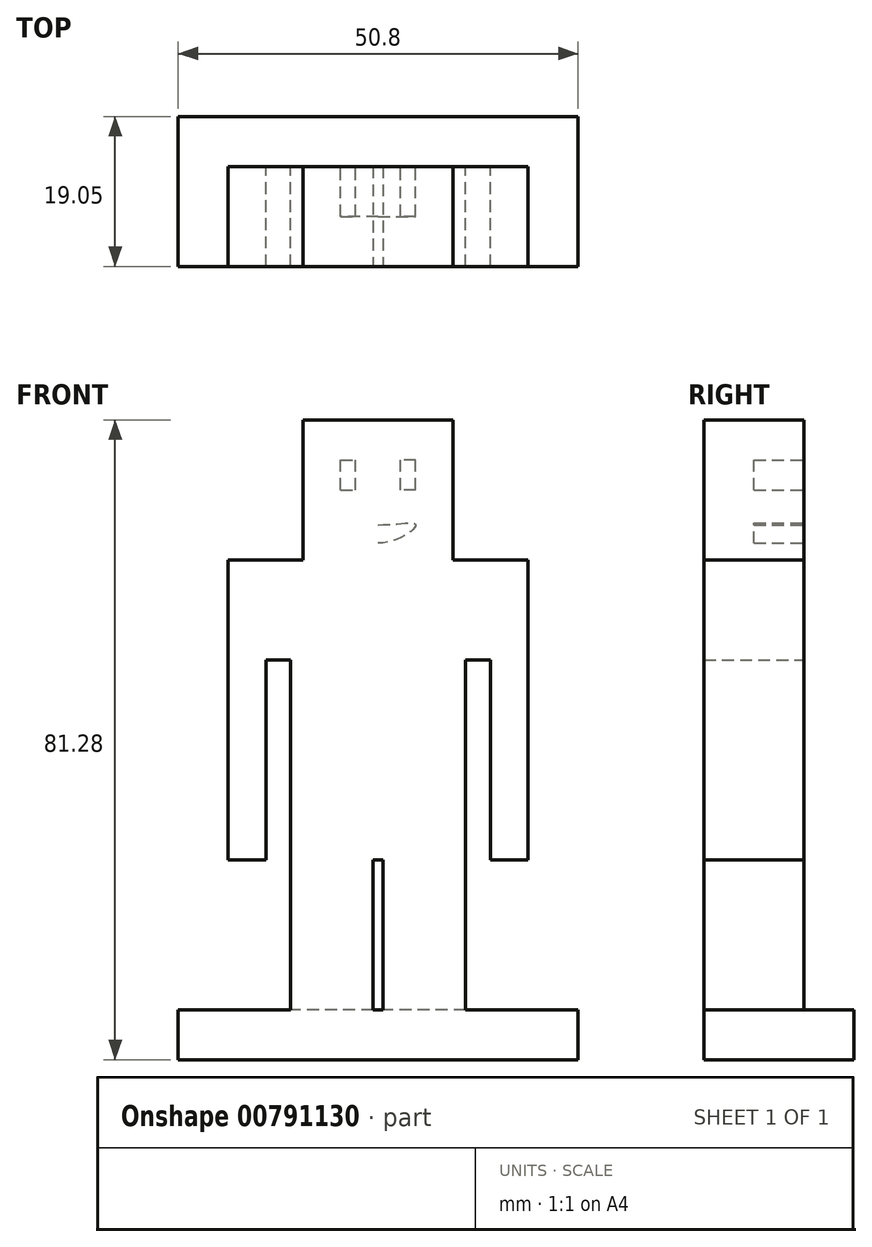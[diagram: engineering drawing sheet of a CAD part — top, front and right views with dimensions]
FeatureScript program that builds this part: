
annotation { "Feature Type Name" : "Feature", "Feature Type Description" : "" }
export const myFeature = defineFeature(function(context is Context, id is Id, definition is map)
    precondition{}
    {
        {
            var Q0;
            Q0=qCreatedBy(makeId("Top.planeOp"),FACE);
            var sketch = newSketch(context, id + "F0", { "sketchPlane" : qUnion([Q0])});
            skLineSegment(sketch, "E0", {"start": v(0, 0) * mm, "end": v(0, -25.4) * mm});
            skLineSegment(sketch, "E1", {"start": v(0, -25.4) * mm, "end": v(50.8, -25.4) * mm});
            skLineSegment(sketch, "E2", {"start": v(50.8, -25.4) * mm, "end": v(50.8, 0) * mm});
            skLineSegment(sketch, "E3", {"start": v(50.8, 0) * mm, "end": v(0, 0) * mm});
            skSolve(sketch);
        }
        {
            var Q0;
            Q0 = qSketchRegion(id + "F0", true);
            extrude(context, id + "F1", {"entities" : qUnion([Q0]), "depth" : 6.35 * mm, "offsetDistance" : 25.4 * mm});
        }
        {
            var Q0;
            Q0=makeQuery(id+"F1.opExtrude","CAP_FACE",FACE,{"disambiguationData":[OSD([sQuery(id+"F0.wireOp",EDGE,"E0"),sQuery(id+"F0.wireOp",EDGE,"E1"),sQuery(id+"F0.wireOp",EDGE,"E2"),sQuery(id+"F0.wireOp",EDGE,"E3")])],"isStart":false});
            var sketch = newSketch(context, id + "F2", { "sketchPlane" : qUnion([Q0])});
            skPoint(sketch, "E4", {"position": v(25.4, -12.7) * mm});
            skPoint(sketch, "E4.positionSnap0", {"position": v(25.4, 0) * mm});
            skPoint(sketch, "E4.positionSnap1", {"position": v(50.8, -12.7) * mm});
            skLineSegment(sketch, "E5.bottom", {"start": v(38.1, -6.35) * mm, "end": v(12.7, -6.35) * mm});
            skLineSegment(sketch, "E5.top", {"start": v(38.1, -19.05) * mm, "end": v(12.7, -19.05) * mm});
            skLineSegment(sketch, "E5.left", {"start": v(38.1, -6.35) * mm, "end": v(38.1, -19.05) * mm});
            skLineSegment(sketch, "E5.right", {"start": v(12.7, -6.35) * mm, "end": v(12.7, -19.05) * mm});
            skLineSegment(sketch, "E6", {"start": v(25.4, -19.05) * mm, "end": v(25.4, -6.35) * mm});
            skSolve(sketch);
        }
        {
            var Q0;
            Q0 = qSketchRegion(id + "F2", true);
            extrude(context, id + "F3", {"entities" : qUnion([Q0]), "operationType" : NewBodyOperationType.ADD, "depth" : 19.05 * mm, "offsetDistance" : 25.4 * mm});
        }
        {
            var Q0;
            Q0=makeQuery(id+"F3.opExtrude","CAP_FACE",FACE,{"disambiguationData":[OSD([sQuery(id+"F2.wireOp",EDGE,"E5.bottom"),sQuery(id+"F2.wireOp",EDGE,"E5.top"),sQuery(id+"F2.wireOp",EDGE,"E5.left"),sQuery(id+"F2.wireOp",EDGE,"E5.right")])],"isStart":false});
            cPlane(context, id + "F4", {"entities" : qUnion([Q0]), "cplaneType" : CPlaneType.OFFSET, "offset" : 0 * mm, "width" : 152.4 * mm, "height" : 152.4 * mm});
        }
        {
            var Q0;
            Q0=qCreatedBy(id+"F4.planeOp",FACE);
            var sketch = newSketch(context, id + "F5", { "sketchPlane" : qUnion([Q0])});
            skLineSegment(sketch, "E7.bottom", {"start": v(44.45, -6.35) * mm, "end": v(6.35, -6.35) * mm});
            skLineSegment(sketch, "E7.top", {"start": v(44.45, -19.05) * mm, "end": v(6.35, -19.05) * mm});
            skLineSegment(sketch, "E7.left", {"start": v(44.45, -6.35) * mm, "end": v(44.45, -19.05) * mm});
            skLineSegment(sketch, "E7.right", {"start": v(6.35, -6.35) * mm, "end": v(6.35, -19.05) * mm});
            skPoint(sketch, "E7.middle", {"position": v(25.4, -12.7) * mm});
            skSolve(sketch);
        }
        {
            var Q0;
            Q0=makeQuery(id+"F5.imprint","IMPRINT",FACE,{"disambiguationData":[TD([[makeQuery(id+"F5.imprint","IMPRINT",EDGE,{"derivedFrom":sQuery(id+"F5.wireOp",EDGE,"E7.bottom")}),1.0]])]});
            extrude(context, id + "F6", {"entities" : qUnion([Q0]), "operationType" : NewBodyOperationType.ADD, "depth" : 38.1 * mm, "offsetDistance" : 25.4 * mm});
        }
        {
            var Q0;
            Q0=makeQuery(id+"F6.opExtrude","CAP_FACE",FACE,{"disambiguationData":[OSD([sQuery(id+"F5.wireOp",EDGE,"E7.bottom"),sQuery(id+"F5.wireOp",EDGE,"E7.top"),sQuery(id+"F5.wireOp",EDGE,"E7.left"),sQuery(id+"F5.wireOp",EDGE,"E7.right")])],"isStart":false});
            var sketch = newSketch(context, id + "F7", { "sketchPlane" : qUnion([Q0])});
            skSolve(sketch);
        }
        {
            var Q0;
            Q0=makeQuery(id+"F7.imprint","IMPRINT",FACE,{"disambiguationData":[TD([[makeQuery(id+"F7.imprint","IMPRINT",EDGE,{"derivedFrom":makeQuery(id+"F6.opExtrude","CAP_EDGE",EDGE,{"disambiguationData":[OSD([sQuery(id+"F5.wireOp",EDGE,"E7.bottom")])],"isStart":false})}),1.0]])]});
            var sketch = newSketch(context, id + "F8", { "sketchPlane" : qUnion([Q0])});
            skLineSegment(sketch, "E8.bottom", {"start": v(34.92, -6.35) * mm, "end": v(15.87, -6.35) * mm});
            skLineSegment(sketch, "E8.top", {"start": v(34.92, -19.05) * mm, "end": v(15.88, -19.05) * mm});
            skLineSegment(sketch, "E8.left", {"start": v(34.92, -6.35) * mm, "end": v(34.92, -19.05) * mm});
            skLineSegment(sketch, "E8.right", {"start": v(15.87, -6.35) * mm, "end": v(15.88, -19.05) * mm});
            skPoint(sketch, "E8.middle", {"position": v(25.4, -12.7) * mm});
            skSolve(sketch);
        }
        {
            var Q0;
            Q0=makeQuery(id+"F8.imprint","IMPRINT",FACE,{"disambiguationData":[TD([[makeQuery(id+"F8.imprint","IMPRINT",EDGE,{"derivedFrom":sQuery(id+"F8.wireOp",EDGE,"E8.bottom")}),1.0]])]});
            extrude(context, id + "F9", {"entities" : qUnion([Q0]), "operationType" : NewBodyOperationType.ADD, "depth" : 17.78 * mm, "offsetDistance" : 25.4 * mm});
        }
        {
            var Q0;
            Q0=makeQuery(id+"F9.boolean.opBoolean","MERGE",FACE,{"derivedFrom":[makeQuery(id+"F6.boolean.opBoolean","MERGE",FACE,{"derivedFrom":[makeQuery(id+"F3.opExtrude","SWEPT_FACE",FACE,{"disambiguationData":[OSD([sQuery(id+"F2.wireOp",EDGE,"E5.top")])]}),makeQuery(id+"F6.opExtrude","SWEPT_FACE",FACE,{"disambiguationData":[OSD([sQuery(id+"F5.wireOp",EDGE,"E7.top")])]})]}),makeQuery(id+"F9.opExtrude","SWEPT_FACE",FACE,{"disambiguationData":[OSD([sQuery(id+"F8.wireOp",EDGE,"E8.top")])]})]});
            var sketch = newSketch(context, id + "F10", { "sketchPlane" : qUnion([Q0])});
            skLineSegment(sketch, "E9", {"start": v(25.4, 6.35) * mm, "end": v(25.4, 25.38) * mm});
            skLineSegment(sketch, "E10.bottom", {"start": v(26.04, 25.4) * mm, "end": v(24.77, 25.4) * mm});
            skLineSegment(sketch, "E10.top", {"start": v(26.04, 6.34) * mm, "end": v(24.77, 6.34) * mm});
            skLineSegment(sketch, "E10.left", {"start": v(26.04, 25.4) * mm, "end": v(26.04, 6.34) * mm});
            skLineSegment(sketch, "E10.right", {"start": v(24.77, 25.4) * mm, "end": v(24.77, 6.34) * mm});
            skPoint(sketch, "E10.middle", {"position": v(25.4, 15.87) * mm});
            skSolve(sketch);
        }
        {
            var Q0;
            Q0 = qSketchRegion(id + "F10", true);
            extrude(context, id + "F11", {"entities" : qUnion([Q0]), "operationType" : NewBodyOperationType.REMOVE, "oppositeDirection" : true, "depth" : 25.4 * mm, "offsetDistance" : 25.4 * mm});
        }
        {
            var Q0;
            Q0=makeQuery(id+"F9.boolean.opBoolean","MERGE",FACE,{"derivedFrom":[makeQuery(id+"F6.boolean.opBoolean","MERGE",FACE,{"derivedFrom":[makeQuery(id+"F3.opExtrude","SWEPT_FACE",FACE,{"disambiguationData":[OSD([sQuery(id+"F2.wireOp",EDGE,"E5.bottom")])]}),makeQuery(id+"F6.opExtrude","SWEPT_FACE",FACE,{"disambiguationData":[OSD([sQuery(id+"F5.wireOp",EDGE,"E7.bottom")])]})]}),makeQuery(id+"F9.opExtrude","SWEPT_FACE",FACE,{"disambiguationData":[OSD([sQuery(id+"F8.wireOp",EDGE,"E8.bottom")])]})]});
            var sketch = newSketch(context, id + "F12", { "sketchPlane" : qUnion([Q0])});
            skLineSegment(sketch, "E11", {"start": v(-38.1, 25.4) * mm, "end": v(-38.1, 50.8) * mm});
            skLineSegment(sketch, "E12", {"start": v(-12.7, 25.4) * mm, "end": v(-12.7, 50.8) * mm});
            skLineSegment(sketch, "E13.bottom", {"start": v(-36.51, 50.8) * mm, "end": v(-39.69, 50.8) * mm});
            skLineSegment(sketch, "E13.top", {"start": v(-36.51, 25.4) * mm, "end": v(-39.69, 25.4) * mm});
            skLineSegment(sketch, "E13.left", {"start": v(-36.51, 50.8) * mm, "end": v(-36.51, 25.4) * mm});
            skLineSegment(sketch, "E13.right", {"start": v(-39.69, 50.8) * mm, "end": v(-39.69, 25.4) * mm});
            skPoint(sketch, "E13.middle", {"position": v(-38.1, 38.1) * mm});
            skLineSegment(sketch, "E14.bottom", {"start": v(-11.16, 50.8) * mm, "end": v(-14.24, 50.8) * mm});
            skLineSegment(sketch, "E14.top", {"start": v(-11.16, 25.4) * mm, "end": v(-14.24, 25.4) * mm});
            skLineSegment(sketch, "E14.left", {"start": v(-11.16, 50.8) * mm, "end": v(-11.16, 25.4) * mm});
            skLineSegment(sketch, "E14.right", {"start": v(-14.24, 50.8) * mm, "end": v(-14.24, 25.4) * mm});
            skPoint(sketch, "E14.middle", {"position": v(-12.7, 38.1) * mm});
            skSolve(sketch);
        }
        {
            var Q0;
            {var subQ0=sQuery(id+"F12.wireOp",EDGE,"E11");Q0=makeQuery(id+"F12.imprint","IMPRINT",FACE,{"disambiguationData":[TD([[makeQuery(id+"F12.imprint","IMPRINT",EDGE,{"derivedFrom":subQ0}),1.0]])]});}
            var Q1;
            {var subQ0=sQuery(id+"F12.wireOp",EDGE,"E12");Q1=makeQuery(id+"F12.imprint","IMPRINT",FACE,{"disambiguationData":[TD([[makeQuery(id+"F12.imprint","IMPRINT",EDGE,{"derivedFrom":subQ0}),-1.0]])]});}
            var Q2;
            {var subQ0=sQuery(id+"F12.wireOp",EDGE,"E11");Q2=makeQuery(id+"F12.imprint","IMPRINT",FACE,{"disambiguationData":[TD([[makeQuery(id+"F12.imprint","IMPRINT",EDGE,{"derivedFrom":subQ0}),-1.0]])]});}
            var Q3;
            {var subQ0=sQuery(id+"F12.wireOp",EDGE,"E12");Q3=makeQuery(id+"F12.imprint","IMPRINT",FACE,{"disambiguationData":[TD([[makeQuery(id+"F12.imprint","IMPRINT",EDGE,{"derivedFrom":subQ0}),1.0]])]});}
            extrude(context, id + "F13", {"entities" : qUnion([Q0, Q1, Q2, Q3]), "operationType" : NewBodyOperationType.REMOVE, "oppositeDirection" : true, "depth" : 50.8 * mm, "offsetDistance" : 25.4 * mm});
        }
        {
            var Q0;
            Q0=makeQuery(id+"F9.boolean.opBoolean","MERGE",FACE,{"derivedFrom":[makeQuery(id+"F6.boolean.opBoolean","MERGE",FACE,{"derivedFrom":[makeQuery(id+"F3.opExtrude","SWEPT_FACE",FACE,{"disambiguationData":[OSD([sQuery(id+"F2.wireOp",EDGE,"E5.bottom")])]}),makeQuery(id+"F6.opExtrude","SWEPT_FACE",FACE,{"disambiguationData":[OSD([sQuery(id+"F5.wireOp",EDGE,"E7.bottom")])]})]}),makeQuery(id+"F9.opExtrude","SWEPT_FACE",FACE,{"disambiguationData":[OSD([sQuery(id+"F8.wireOp",EDGE,"E8.bottom")])]})]});
            var sketch = newSketch(context, id + "F14", { "sketchPlane" : qUnion([Q0])});
            skLineSegment(sketch, "E15", {"start": v(-34.92, 63.5) * mm, "end": v(-15.88, 63.5) * mm});
            skPoint(sketch, "E16", {"position": v(-25.4, 72.4) * mm});
            skLineSegment(sketch, "E17", {"start": v(-34.92, 72.4) * mm, "end": v(-25.4, 72.4) * mm});
            skLineSegment(sketch, "E18", {"start": v(-15.87, 72.4) * mm, "end": v(-25.4, 72.4) * mm});
            skLineSegment(sketch, "E19.bottom", {"start": v(-30.16, 72.4) * mm, "end": v(-28.26, 72.4) * mm});
            skLineSegment(sketch, "E19.top", {"start": v(-30.16, 76.2) * mm, "end": v(-28.26, 76.2) * mm});
            skLineSegment(sketch, "E19.left", {"start": v(-30.16, 72.4) * mm, "end": v(-30.16, 76.2) * mm});
            skLineSegment(sketch, "E19.right", {"start": v(-28.26, 72.4) * mm, "end": v(-28.26, 76.2) * mm});
            skLineSegment(sketch, "E20.bottom", {"start": v(-20.64, 72.4) * mm, "end": v(-22.54, 72.4) * mm});
            skLineSegment(sketch, "E20.top", {"start": v(-20.64, 76.2) * mm, "end": v(-22.54, 76.2) * mm});
            skLineSegment(sketch, "E20.left", {"start": v(-20.64, 72.4) * mm, "end": v(-20.64, 76.2) * mm});
            skLineSegment(sketch, "E20.right", {"start": v(-22.54, 72.4) * mm, "end": v(-22.54, 76.2) * mm});
            skLineSegment(sketch, "E21", {"start": v(-25.4, 63.5) * mm, "end": v(-25.4, 72.4) * mm});
            skLineSegment(sketch, "E22", {"start": v(-25.4, 81.28) * mm, "end": v(-25.4, 72.4) * mm});
            skPoint(sketch, "E23.0.internal.snap0", {"position": v(-25.4, 67.95) * mm});
            skPoint(sketch, "E23.2.internal.snap0", {"position": v(-25.4, 67.95) * mm});
            skFitSpline(sketch, "E23", {"points": [v(-30.16, 67.95) * mm, v(-25.4, 65.62) * mm, v(-20.64, 67.95) * mm, v(-25.4, 67.95) * mm, v(-30.16, 67.95) * mm]});
            skSolve(sketch);
        }
        {
            var Q0;
            Q0 = qSketchRegion(id + "F14", true);
            extrude(context, id + "F15", {"entities" : qUnion([Q0]), "operationType" : NewBodyOperationType.REMOVE, "oppositeDirection" : true, "depth" : 6.35 * mm, "offsetDistance" : 25.4 * mm});
        }
        {
            var Q0;
            Q0=makeQuery(id+"F9.boolean.opBoolean","MERGE",FACE,{"derivedFrom":[makeQuery(id+"F6.boolean.opBoolean","MERGE",FACE,{"derivedFrom":[makeQuery(id+"F3.opExtrude","SWEPT_FACE",FACE,{"disambiguationData":[OSD([sQuery(id+"F2.wireOp",EDGE,"E5.bottom")])]}),makeQuery(id+"F6.opExtrude","SWEPT_FACE",FACE,{"disambiguationData":[OSD([sQuery(id+"F5.wireOp",EDGE,"E7.bottom")])]})]}),makeQuery(id+"F9.opExtrude","SWEPT_FACE",FACE,{"disambiguationData":[OSD([sQuery(id+"F8.wireOp",EDGE,"E8.bottom")])]})]});
            var sketch = newSketch(context, id + "F16", { "sketchPlane" : qUnion([Q0])});
            skLineSegment(sketch, "E24", {"start": v(-36.51, 25.4) * mm, "end": v(-36.51, 6.35) * mm});
            skLineSegment(sketch, "E25", {"start": v(-36.51, 6.35) * mm, "end": v(-38.1, 6.35) * mm});
            skLineSegment(sketch, "E26", {"start": v(-38.1, 6.35) * mm, "end": v(-38.1, 25.4) * mm});
            skLineSegment(sketch, "E27", {"start": v(-38.1, 25.4) * mm, "end": v(-36.51, 25.4) * mm});
            skLineSegment(sketch, "E28", {"start": v(-12.7, 25.4) * mm, "end": v(-12.7, 6.35) * mm});
            skLineSegment(sketch, "E29", {"start": v(-12.7, 6.35) * mm, "end": v(-14.24, 6.35) * mm});
            skLineSegment(sketch, "E30", {"start": v(-14.24, 6.35) * mm, "end": v(-14.24, 25.4) * mm});
            skLineSegment(sketch, "E31", {"start": v(-14.24, 25.4) * mm, "end": v(-12.7, 25.4) * mm});
            skSolve(sketch);
        }
        {
            var Q0;
            Q0 = qSketchRegion(id + "F16", true);
            extrude(context, id + "F17", {"entities" : qUnion([Q0]), "operationType" : NewBodyOperationType.REMOVE, "oppositeDirection" : true, "depth" : 25.4 * mm, "offsetDistance" : 25.4 * mm});
        }
        {
            var Q0;
            Q0=makeQuery(id+"F1.opExtrude","SWEPT_FACE",FACE,{"disambiguationData":[OSD([sQuery(id+"F0.wireOp",EDGE,"E2")])]});
            var sketch = newSketch(context, id + "F18", { "sketchPlane" : qUnion([Q0])});
            skLineSegment(sketch, "E32.0.0", {"start": v(-25.4, 0) * mm, "end": v(0, 0) * mm});
            skLineSegment(sketch, "E32.0.1", {"start": v(0, 0) * mm, "end": v(0, 6.35) * mm});
            skLineSegment(sketch, "E32.0.2", {"start": v(0, 6.35) * mm, "end": v(-25.4, 6.35) * mm});
            skLineSegment(sketch, "E32.0.3", {"start": v(-25.4, 6.35) * mm, "end": v(-25.4, 0) * mm});
            skLineSegment(sketch, "E33.0", {"start": v(-19.05, 6.35) * mm, "end": v(-19.05, 50.8) * mm});
            skLineSegment(sketch, "E34", {"start": v(-19.05, 6.35) * mm, "end": v(-19.05, 0) * mm});
            skSolve(sketch);
        }
        {
            var Q0;
            {var subQ0=sQuery(id+"F18.wireOp",EDGE,"E32.0.3");Q0=makeQuery(id+"F18.imprint","IMPRINT",FACE,{"disambiguationData":[TD([[makeQuery(id+"F18.imprint","IMPRINT",EDGE,{"derivedFrom":subQ0}),1.0]])]});}
            extrude(context, id + "F19", {"entities" : qUnion([Q0]), "operationType" : NewBodyOperationType.REMOVE, "endBound" : BoundingType.THROUGH_ALL, "oppositeDirection" : true, "depth" : 25.4 * mm, "offsetDistance" : 25.4 * mm});
        }
    });
